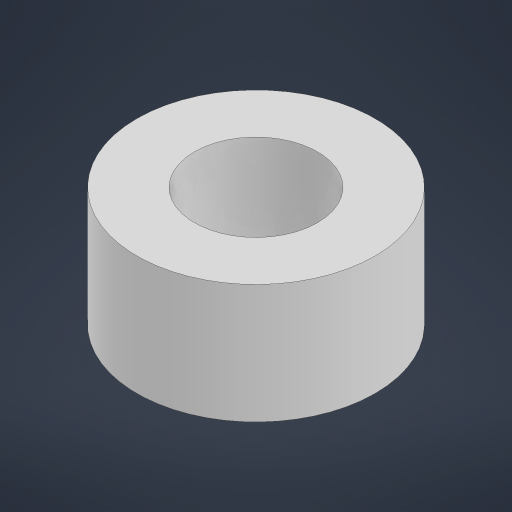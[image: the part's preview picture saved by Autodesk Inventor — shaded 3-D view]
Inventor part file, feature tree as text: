
AUTODESK INVENTOR PART (.ipt)
format: ipt  version: 2024 (Build 280153000, 153)  size: 153,088 bytes
history: native  units: in
note: dims shown in document units (in); Inventor stores cm internally (conversion verified against a paired STEP export)
features: extrude x1, sketch x1
ambient origin geometry x8: Origin, YZ Plane, XZ Plane, XY Plane, X Axis, Y Axis, Z Axis, Center Point
bodies: Solid1 (feature_tree)
feature tree (2):
  extrude  "Extrusion1"  Depth=0.1181in
  sketch  "Sketch1"  dims[d0=0.122in d1=0.2362in d2=0.1181in d3=0.0in]
